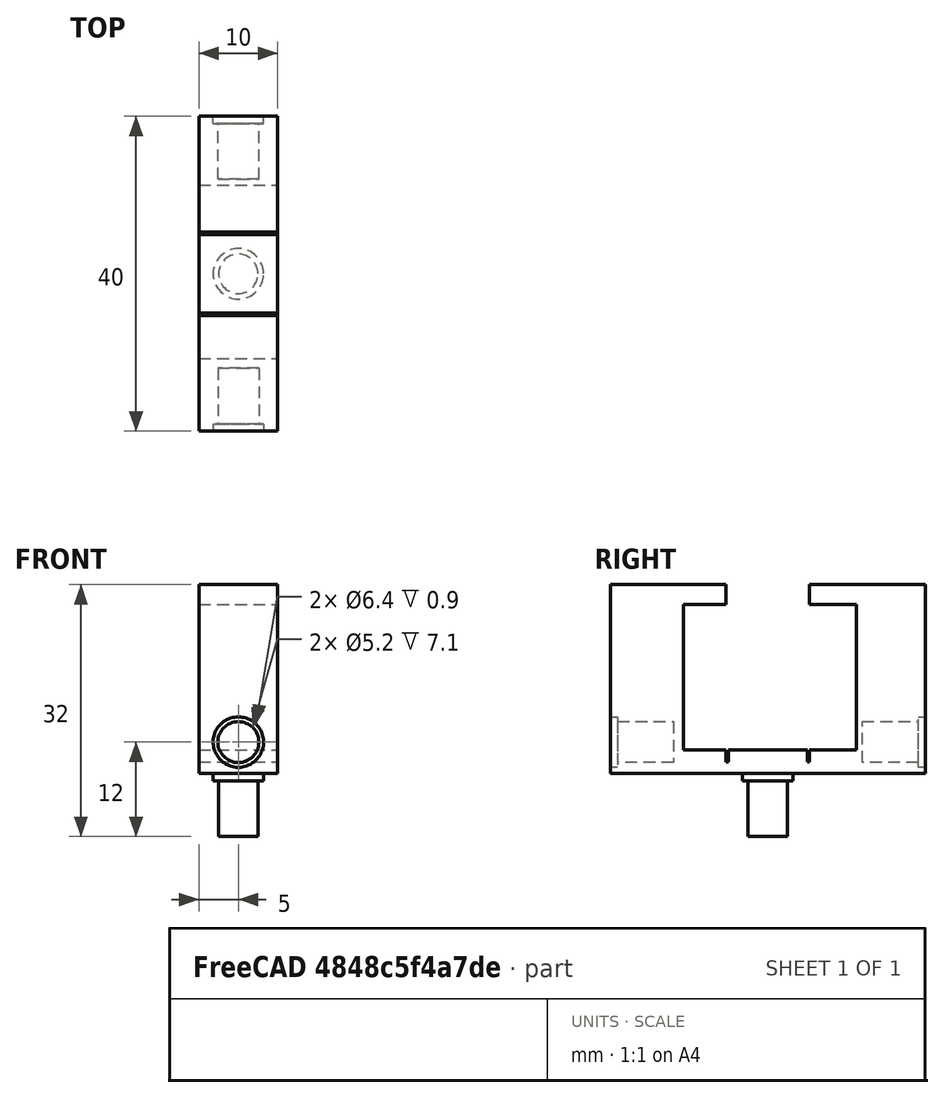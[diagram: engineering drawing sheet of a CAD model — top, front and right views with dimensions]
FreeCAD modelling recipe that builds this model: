
FCSTD DOCUMENT  (FreeCAD 0.20R29177 +426 (Git))
Label: motorHolder
License: All rights reserved
LicenseURL: http://en.wikipedia.org/wiki/All_rights_reserved
objects: Part::MultiFuse×7, Part::Cylinder×6, Part::Box×5, Part::Cut×2, Mesh::Feature×2
note: 20 computed .brp shape members not serialized (recipe doc carries the construction recipe); baked Part::Feature solids carry a one-line shape summary decoded from their .brp

FEATURE [Part::Cylinder] Cylinder
  Angle = 360
  AttacherType = Attacher::AttachEngine3D
  FirstAngle = 0
  Height = 1.8
  Placement = pos=(-0.9,0,0) rot=(0,1,0;1.5708rad)
  Radius = 3.2
  SecondAngle = 0
FEATURE [Part::Cylinder] Cylinder001
  Angle = 360
  AttacherType = Attacher::AttachEngine3D
  FirstAngle = 0
  Height = 8
  Placement = pos=(0,0,0) rot=(0,1,0;1.5708rad)
  Radius = 2.51
  SecondAngle = 0
FEATURE [Part::MultiFuse] Fusion  label="pin"
  Placement = pos=(0,0,0) rot=(0,1,0;1.5708rad)
  Shapes = -> [Cylinder,Cylinder001]
FEATURE [Part::Box] Box  label="Cube"
  AttacherType = Attacher::AttachEngine3D
  Height = 3
  Length = 10
  Placement = pos=(-5,-5,0) rot=(0,0,1;0rad)
  Width = 10
FEATURE [Part::Box] Box001  label="Cube001"
  AttacherType = Attacher::AttachEngine3D
  Height = 1.5
  Length = 10
  Placement = pos=(-5,-20,0) rot=(0,0,1;0rad)
  Width = 40
FEATURE [Part::MultiFuse] Fusion001
  Shapes = -> [Fusion,Box,Box001]
FEATURE [Part::Cylinder] Cylinder002
  Angle = 360
  AttacherType = Attacher::AttachEngine3D
  FirstAngle = 0
  Height = 1.8
  Placement = pos=(-0.9,0,0) rot=(0,1,0;1.5708rad)
  Radius = 3.2
  SecondAngle = 0
FEATURE [Part::Cylinder] Cylinder003
  Angle = 360
  AttacherType = Attacher::AttachEngine3D
  FirstAngle = 0
  Height = 8
  Placement = pos=(0,0,0) rot=(0,1,0;1.5708rad)
  Radius = 2.6
  SecondAngle = 0
FEATURE [Part::MultiFuse] Fusion002  label="pin001"
  Placement = pos=(0,-20,4) rot=(0.707107,0.707107,0;3.14159rad)
  Shapes = -> [Cylinder002,Cylinder003]
FEATURE [Part::Cylinder] Cylinder004
  Angle = 360
  AttacherType = Attacher::AttachEngine3D
  FirstAngle = 0
  Height = 1.8
  Placement = pos=(-0.9,0,0) rot=(0,1,0;1.5708rad)
  Radius = 3.2
  SecondAngle = 0
FEATURE [Part::Cylinder] Cylinder005
  Angle = 360
  AttacherType = Attacher::AttachEngine3D
  FirstAngle = 0
  Height = 8
  Placement = pos=(0,0,0) rot=(0,1,0;1.5708rad)
  Radius = 2.6
  SecondAngle = 0
FEATURE [Part::MultiFuse] Fusion003  label="pin002"
  Placement = pos=(0,20,4) rot=(0,0,1;4.71239rad)
  Shapes = -> [Cylinder004,Cylinder005]
FEATURE [Part::Box] Box002  label="Cube002"
  AttacherType = Attacher::AttachEngine3D
  Height = 24
  Length = 10
  Placement = pos=(-5,5.3,0) rot=(0,0,1;0rad)
  Width = 14.7
FEATURE [Part::MultiFuse] Fusion004  label="pins"
  Shapes = -> [Fusion002,Fusion003]
FEATURE [Part::Box] Box003  label="Cube003"
  AttacherType = Attacher::AttachEngine3D
  Height = 24
  Length = 10
  Placement = pos=(-5,-20,0) rot=(0,0,1;0rad)
  Width = 14.7
FEATURE [Part::Box] Box004  label="motor"
  AttacherType = Attacher::AttachEngine3D
  Height = 22
  Length = 50
  Placement = pos=(-13,11.25,3) rot=(1,0,0;1.5708rad)
  Width = 18.5
FEATURE [Part::MultiFuse] Fusion005
  Shapes = -> [Box002,Box003]
FEATURE [Part::Cut] Cut
  Base = -> Fusion005
  Tool = -> Box004
FEATURE [Part::MultiFuse] Fusion006
  Shapes = -> [Cut,Fusion001]
FEATURE [Part::Cut] Cut001
  Base = -> Fusion006
  Tool = -> Fusion004
FEATURE [Mesh::Feature] _749  label="3749"
  Placement = pos=(0,20,4) rot=(0,0,1;1.5708rad)
FEATURE [Mesh::Feature] _750  label="3749001"
  Placement = pos=(0,-20,4) rot=(0,0,1;4.71239rad)
